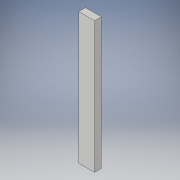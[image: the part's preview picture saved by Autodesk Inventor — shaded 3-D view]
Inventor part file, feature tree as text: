
AUTODESK INVENTOR PART (.ipt)
format: ipt  version: 2017 (Build 210142000, 142)  size: 91,648 bytes
history: native  units: in
note: dims shown in document units (in); Inventor stores cm internally (conversion verified against a paired STEP export)
features: extrude x1, sketch x1
ambient origin geometry x8: Origin, YZ Plane, XZ Plane, XY Plane, X Axis, Y Axis, Z Axis, Center Point
bodies: Solid1 (feature_tree)
feature tree (2):
  extrude  "Extrusion1"  Depth=1.5in
  sketch  "Sketch1"  dims[d0=3.5in d1=1.5in d2=29.0in d3=0.0in]
